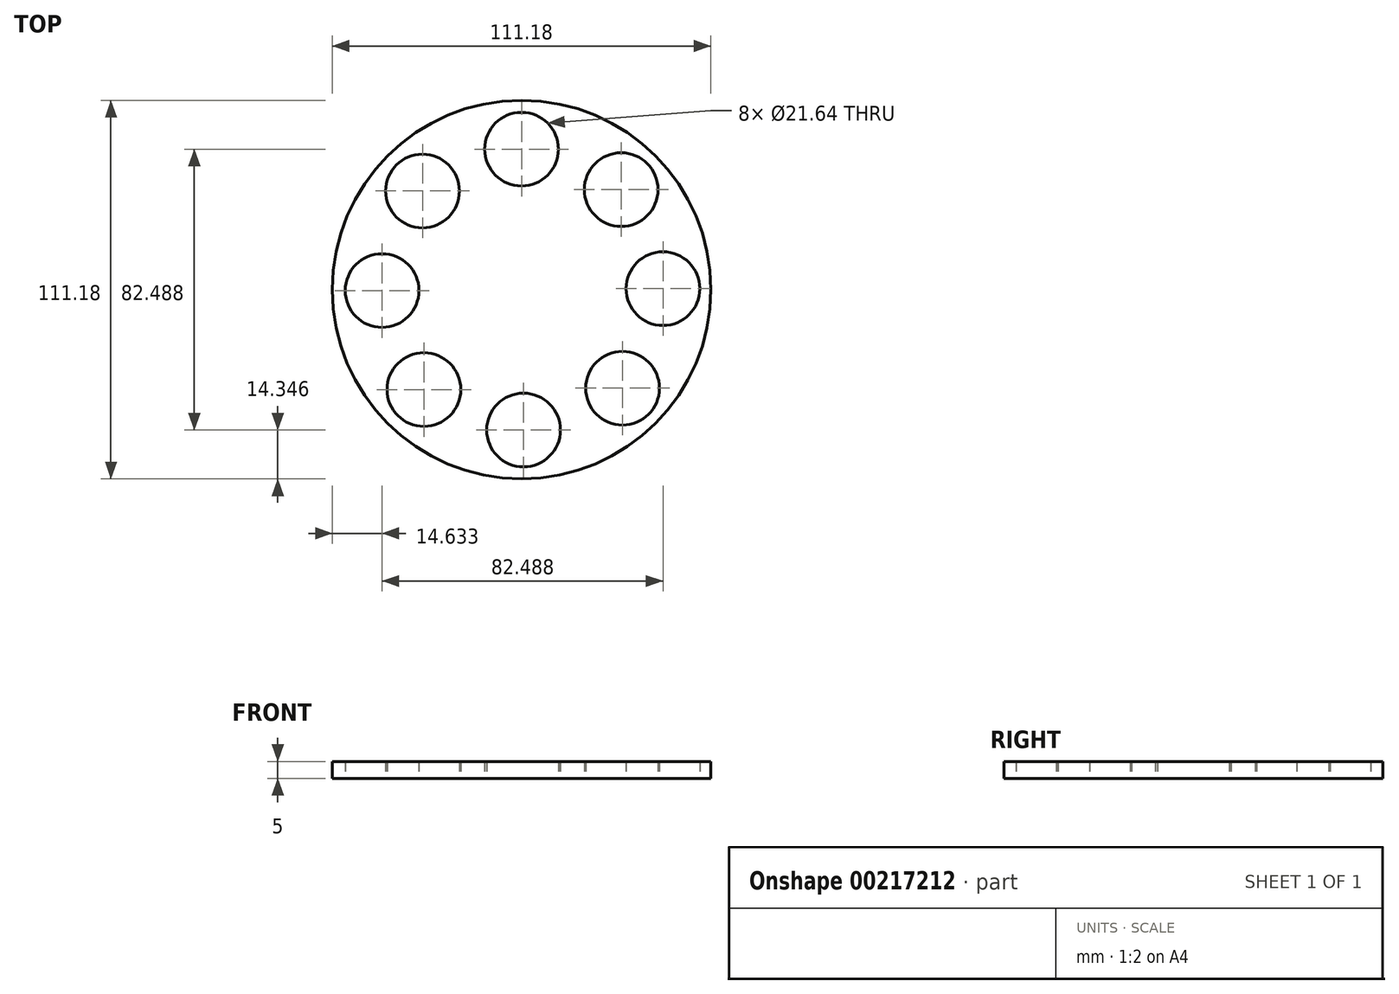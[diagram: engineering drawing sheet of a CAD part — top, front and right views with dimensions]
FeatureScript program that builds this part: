
annotation { "Feature Type Name" : "Feature", "Feature Type Description" : "" }
export const myFeature = defineFeature(function(context is Context, id is Id, definition is map)
    precondition{}
    {
        {
            var Q0;
            Q0=qCreatedBy(makeId("Top.planeOp"),FACE);
            var sketch = newSketch(context, id + "F0", { "sketchPlane" : qUnion([Q0])});
            skCircle(sketch, "E0", {"center": v(0, 0) * mm, "radius": 55.59 * mm});
            skCircle(sketch, "E1", {"center": v(0, 41.24) * mm, "radius": 10.82 * mm});
            skCircle(sketch, "E2.1.0", {"center": v(-29.08, 28.96) * mm, "radius": 10.82 * mm});
            skCircle(sketch, "E2.2.0", {"center": v(-40.96, -0.29) * mm, "radius": 10.82 * mm});
            skCircle(sketch, "E2.3.0", {"center": v(-28.67, -29.37) * mm, "radius": 10.82 * mm});
            skCircle(sketch, "E2.4.0", {"center": v(0.57, -41.24) * mm, "radius": 10.82 * mm});
            skCircle(sketch, "E2.5.0", {"center": v(29.65, -28.96) * mm, "radius": 10.82 * mm});
            skCircle(sketch, "E2.6.0", {"center": v(41.53, 0.29) * mm, "radius": 10.82 * mm});
            skCircle(sketch, "E2.7.0", {"center": v(29.25, 29.37) * mm, "radius": 10.82 * mm});
            skPoint(sketch, "E2.center", {"position": v(0.29, 0) * mm});
            skSolve(sketch);
        }
        {
            var Q0;
            Q0=makeQuery(id+"F0.imprint","IMPRINT",FACE,{"disambiguationData":[TD([[makeQuery(id+"F0.imprint","IMPRINT",EDGE,{"derivedFrom":sQuery(id+"F0.wireOp",EDGE,"E0")}),1.0]])]});
            extrude(context, id + "F1", {"entities" : qUnion([Q0]), "depth" : 5 * mm});
        }
    });
